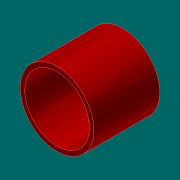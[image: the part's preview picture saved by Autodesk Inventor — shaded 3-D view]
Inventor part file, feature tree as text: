
AUTODESK INVENTOR PART (.ipt)
format: ipt  version: 2017.3 (Build 213257000, 257)  size: 97,792 bytes
history: native  units: in
note: dims shown in document units (in); Inventor stores cm internally (conversion verified against a paired STEP export)
features: other x3, extrude x2, sketch x2
ambient origin geometry x8: Origin, YZ Plane, XZ Plane, XY Plane, X Axis, Y Axis, Z Axis, Center Point
bodies: Solid1 (feature_tree)
feature tree (7):
  other  "A1-19027-400-09 HCWI liner - drain.ipt"
  extrude  "Extrusion1"  Depth=0.5in TaperAngle=0.0deg
  extrude  "Extrusion2"  [1 undecoded]
  other  "Solid1::A1-19027-400-09 HCWI liner - drain.ipt"
  other  "TaggingFeature1"
  sketch  "Sketch2"  dims[d0=0.3937in d1=0.5in d2=0.5in d3=0.0in d4=0.0in]
  sketch  "Sketch3"  dims[d5=0.5in d6=1.0in d7=0.0in d8=0.0in]
note: 1 required parameter value undecoded (feature->parameter linkage not recoverable at this tier; creation-order binding heuristic only, values carry confidence <= 0.55)
